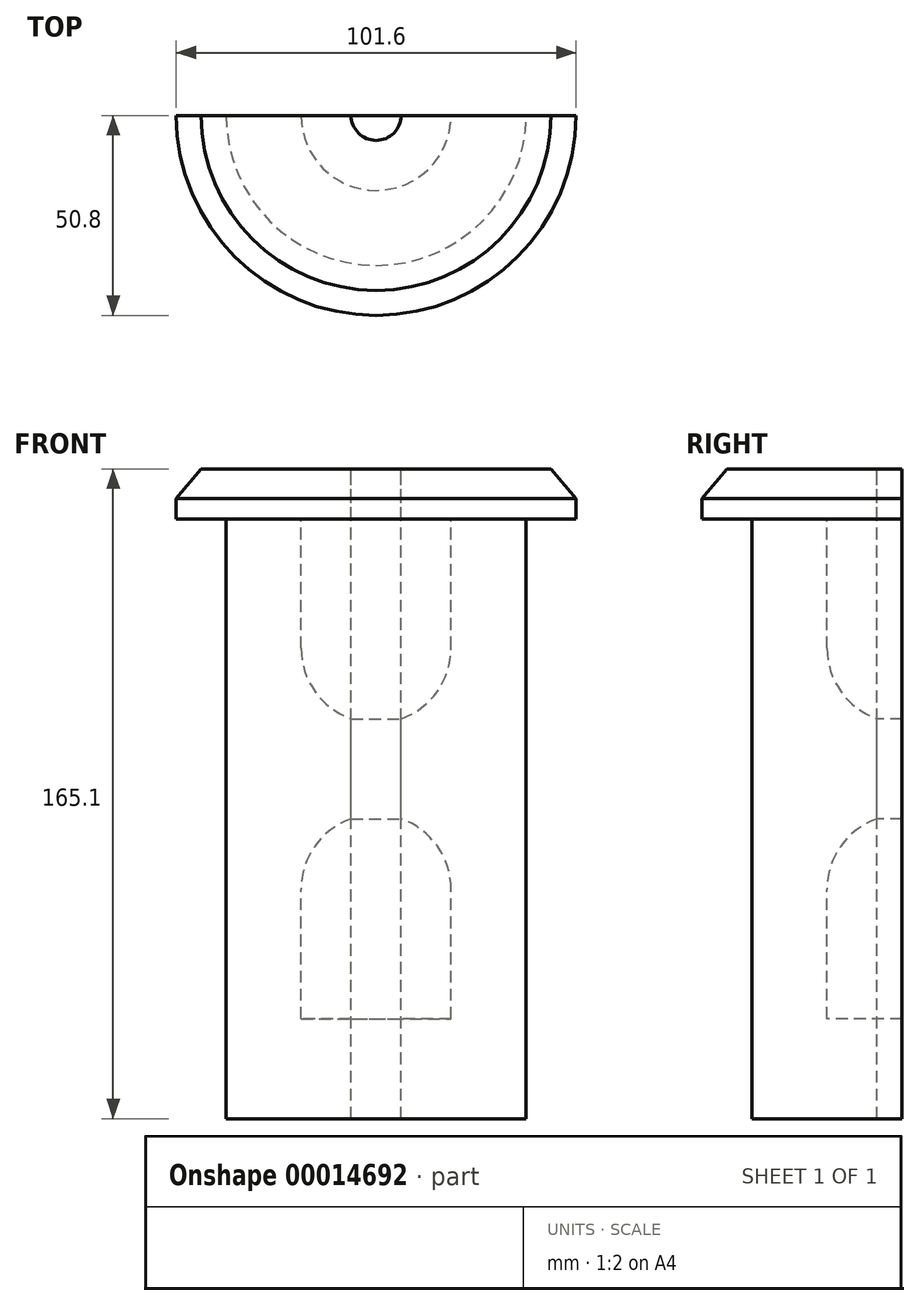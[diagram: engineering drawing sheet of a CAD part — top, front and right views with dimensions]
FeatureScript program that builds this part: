
annotation { "Feature Type Name" : "Feature", "Feature Type Description" : "" }
export const myFeature = defineFeature(function(context is Context, id is Id, definition is map)
    precondition{}
    {
        {
            var Q0;
            Q0=qCreatedBy(makeId("Front.planeOp"),FACE);
            var sketch = newSketch(context, id + "F0", { "sketchPlane" : qUnion([Q0])});
            skLineSegment(sketch, "E0", {"start": v(38.1, 119.47) * mm, "end": v(38.1, -168.69) * mm, "construction": true});
            skLineSegment(sketch, "E1", {"start": v(0, 139.05) * mm, "end": v(0, -174.75) * mm, "construction": true});
            skLineSegment(sketch, "E2", {"start": v(12.7, 126.35) * mm, "end": v(12.7, -144.59) * mm, "construction": true});
            skLineSegment(sketch, "E3", {"start": v(19.05, 145.3) * mm, "end": v(19.05, -141.5) * mm, "construction": true});
            skLineSegment(sketch, "E4", {"start": v(38.1, 63.5) * mm, "end": v(38.1, -63.5) * mm});
            skPoint(sketch, "E5", {"position": v(38.1, 0) * mm});
            skLineSegment(sketch, "E6", {"start": v(38.1, 63.5) * mm, "end": v(19.05, 63.5) * mm});
            skLineSegment(sketch, "E7", {"start": v(19.05, 63.5) * mm, "end": v(19.05, 30.66) * mm});
            skLineSegment(sketch, "E8", {"start": v(0, 0) * mm, "end": v(253.77, 0) * mm, "construction": true});
            skArc(sketch, "E9", {"start": v(19.05, 30.66) * mm, "mid": v(13.47, 17.2) * mm, "end": v(0, 11.61) * mm});
            skLineSegment(sketch, "E10", {"start": v(6.35, 12.7) * mm, "end": v(6.35, 0) * mm});
            skLineSegment(sketch, "E11.MirrorCS", {"start": v(19.05, -63.5) * mm, "end": v(19.05, -30.66) * mm});
            skArc(sketch, "E12.MirrorCS", {"start": v(19.05, -30.66) * mm, "mid": v(13.47, -17.2) * mm, "end": v(0, -11.61) * mm});
            skLineSegment(sketch, "E13.MirrorCS", {"start": v(6.35, -12.7) * mm, "end": v(6.35, 0) * mm});
            skLineSegment(sketch, "E14.MirrorCS", {"start": v(38.1, -63.5) * mm, "end": v(19.05, -63.5) * mm});
            skPoint(sketch, "E15", {"position": v(19.05, 47.08) * mm});
            skPoint(sketch, "E16", {"position": v(19.05, -47.08) * mm});
            skPoint(sketch, "E17", {"position": v(19.05, 88.9) * mm});
            skLineSegment(sketch, "E18", {"start": v(0, 11.61) * mm, "end": v(0, -11.61) * mm});
            skLineSegment(sketch, "E19", {"start": v(55.1, 63.5) * mm, "end": v(44.45, 76.2) * mm});
            skLineSegment(sketch, "E20", {"start": v(55.1, 63.5) * mm, "end": v(6.35, 63.5) * mm});
            skLineSegment(sketch, "E21", {"start": v(6.35, 63.5) * mm, "end": v(6.35, 12.7) * mm});
            skLineSegment(sketch, "E22", {"start": v(44.45, 76.2) * mm, "end": v(0, 76.2) * mm});
            skLineSegment(sketch, "E23", {"start": v(0, 76.2) * mm, "end": v(0, 11.61) * mm});
            skLineSegment(sketch, "E24", {"start": v(6.35, 63.5) * mm, "end": v(0, 63.5) * mm});
            skLineSegment(sketch, "E25", {"start": v(6.35, -12.7) * mm, "end": v(6.35, -63.5) * mm});
            skLineSegment(sketch, "E26", {"start": v(6.35, -63.5) * mm, "end": v(0, -63.5) * mm});
            skLineSegment(sketch, "E27", {"start": v(0, -63.5) * mm, "end": v(0, -11.61) * mm});
            skLineSegment(sketch, "E28.bottom", {"start": v(38.1, -63.5) * mm, "end": v(0, -63.5) * mm});
            skLineSegment(sketch, "E28.top", {"start": v(38.1, -88.9) * mm, "end": v(0, -88.9) * mm});
            skLineSegment(sketch, "E28.left", {"start": v(38.1, -63.5) * mm, "end": v(38.1, -88.9) * mm});
            skLineSegment(sketch, "E28.right", {"start": v(0, -63.5) * mm, "end": v(0, -88.9) * mm});
            skLineSegment(sketch, "E29", {"start": v(6.35, 63.5) * mm, "end": v(6.35, 76.2) * mm});
            skLineSegment(sketch, "E30", {"start": v(6.35, -63.5) * mm, "end": v(6.35, -88.9) * mm});
            skSolve(sketch);
        }
        {
            var Q0;
            {var subQ5=sQuery(id+"F0.wireOp",EDGE,"E4");Q0=makeQuery(id+"F0.imprint","IMPRINT",FACE,{"disambiguationData":[TD([[makeQuery(id+"F0.imprint","IMPRINT",EDGE,{"derivedFrom":subQ5}),-1.0]])]});}
            var Q1;
            {var subQ2=sQuery(id+"F0.wireOp",EDGE,"E19");Q1=makeQuery(id+"F0.imprint","IMPRINT",FACE,{"disambiguationData":[TD([[makeQuery(id+"F0.imprint","IMPRINT",EDGE,{"derivedFrom":subQ2}),1.0]])]});}
            var Q2;
            {var subQ3=sQuery(id+"F0.wireOp",EDGE,"E28.left");Q2=makeQuery(id+"F0.imprint","IMPRINT",FACE,{"disambiguationData":[TD([[makeQuery(id+"F0.imprint","IMPRINT",EDGE,{"derivedFrom":subQ3}),-1.0]])]});}
            var Q3;
            Q3=sQuery(id+"F0.wireOp",EDGE,"E23");
            revolve(context, id + "F1", {"entities" : qUnion([Q0, Q1, Q2]), "axis" : qUnion([Q3]), "revolveType" : RevolveType.FULL});
        }
        {
            var Q0;
            {var subQ1=sQuery(id+"F0.wireOp",EDGE,"E24");Q0=makeQuery(id+"F0.imprint","IMPRINT",FACE,{"disambiguationData":[TD([[makeQuery(id+"F0.imprint","IMPRINT",EDGE,{"derivedFrom":subQ1}),-1.0]])]});}
            var Q1;
            {var subQ1=sQuery(id+"F0.wireOp",EDGE,"E21");Q1=makeQuery(id+"F0.imprint","IMPRINT",FACE,{"disambiguationData":[TD([[makeQuery(id+"F0.imprint","IMPRINT",EDGE,{"derivedFrom":subQ1}),-1.0]])]});}
            var Q2;
            {var subQ2=sQuery(id+"F0.wireOp",EDGE,"E10");Q2=makeQuery(id+"F0.imprint","IMPRINT",FACE,{"disambiguationData":[TD([[makeQuery(id+"F0.imprint","IMPRINT",EDGE,{"derivedFrom":subQ2}),-1.0]])]});}
            var Q3;
            {var subQ2=sQuery(id+"F0.wireOp",EDGE,"E25");Q3=makeQuery(id+"F0.imprint","IMPRINT",FACE,{"disambiguationData":[TD([[makeQuery(id+"F0.imprint","IMPRINT",EDGE,{"derivedFrom":subQ2}),-1.0]])]});}
            var Q4;
            {var subQ1=sQuery(id+"F0.wireOp",EDGE,"E28.right");Q4=makeQuery(id+"F0.imprint","IMPRINT",FACE,{"disambiguationData":[TD([[makeQuery(id+"F0.imprint","IMPRINT",EDGE,{"derivedFrom":subQ1}),1.0]])]});}
            var Q5;
            Q5=sQuery(id+"F0.wireOp",EDGE,"E23");
            revolve(context, id + "F2", {"entities" : qUnion([Q0, Q1, Q2, Q3, Q4]), "axis" : qUnion([Q5]), "revolveType" : RevolveType.FULL});
        }
        {
            var Q0;
            Q0=qCreatedBy(makeId("Top.planeOp"),FACE);
            var sketch = newSketch(context, id + "F3", { "sketchPlane" : qUnion([Q0])});
            skCircle(sketch, "E31", {"center": v(0, 0) * mm, "radius": 50.8 * mm});
            skCircle(sketch, "E32", {"center": v(0, 0) * mm, "radius": 63.5 * mm});
            skSolve(sketch);
        }
        {
            var Q0;
            Q0=makeQuery(id+"F3.imprint","IMPRINT",FACE,{"disambiguationData":[TD([[makeQuery(id+"F3.imprint","IMPRINT",EDGE,{"derivedFrom":sQuery(id+"F3.wireOp",EDGE,"E31")}),-1.0]])]});
            extrude(context, id + "F4", {"entities" : qUnion([Q0]), "operationType" : NewBodyOperationType.REMOVE, "endBound" : BoundingType.THROUGH_ALL, "depth" : 292 * mm});
        }
        {
            var Q0;
            Q0=qCreatedBy(makeId("Front.planeOp"),FACE);
            var sketch = newSketch(context, id + "F5", { "sketchPlane" : qUnion([Q0])});
            skLineSegment(sketch, "E33.bottom", {"start": v(-118.73, 184.85) * mm, "end": v(169.4, 184.85) * mm});
            skLineSegment(sketch, "E33.top", {"start": v(-118.73, -205.01) * mm, "end": v(169.4, -205.01) * mm});
            skLineSegment(sketch, "E33.left", {"start": v(-118.73, 184.85) * mm, "end": v(-118.73, -205.01) * mm});
            skLineSegment(sketch, "E33.right", {"start": v(169.4, 184.85) * mm, "end": v(169.4, -205.01) * mm});
            skSolve(sketch);
        }
        {
            var Q0;
            Q0=makeQuery(id+"F5.imprint","IMPRINT",FACE,{"disambiguationData":[TD([[makeQuery(id+"F5.imprint","IMPRINT",EDGE,{"derivedFrom":sQuery(id+"F5.wireOp",EDGE,"E33.bottom")}),-1.0]])]});
            extrude(context, id + "F6", {"entities" : qUnion([Q0]), "operationType" : NewBodyOperationType.REMOVE, "endBound" : BoundingType.THROUGH_ALL, "oppositeDirection" : true, "depth" : 25.4 * mm});
        }
    });
